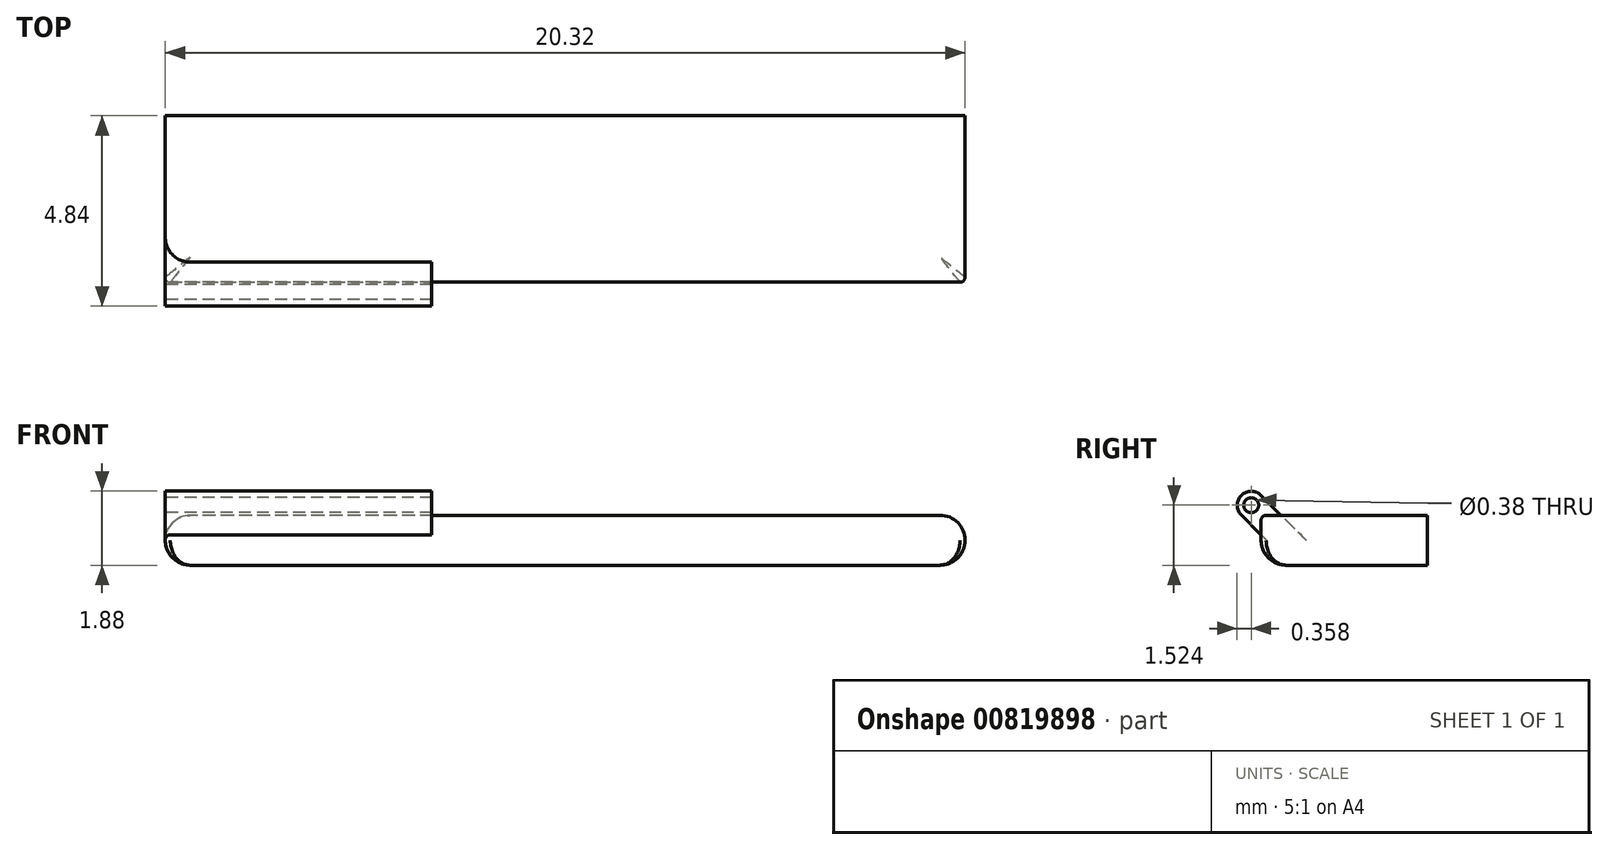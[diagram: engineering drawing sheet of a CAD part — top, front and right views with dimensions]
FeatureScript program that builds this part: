
annotation { "Feature Type Name" : "Feature", "Feature Type Description" : "" }
export const myFeature = defineFeature(function(context is Context, id is Id, definition is map)
    precondition{}
    {
        {
            var Q0;
            Q0=qCreatedBy(makeId("Top.planeOp"),FACE);
            var sketch = newSketch(context, id + "F0", { "sketchPlane" : qUnion([Q0])});
            skLineSegment(sketch, "E0.bottom", {"start": v(0, 0) * mm, "end": v(20.32, 0) * mm});
            skLineSegment(sketch, "E0.top", {"start": v(0, 8.46) * mm, "end": v(20.32, 8.46) * mm});
            skLineSegment(sketch, "E0.left", {"start": v(0, 0) * mm, "end": v(0, 8.46) * mm});
            skLineSegment(sketch, "E0.right", {"start": v(20.32, 0) * mm, "end": v(20.32, 8.46) * mm});
            skSolve(sketch);
        }
        {
            var Q0;
            Q0=qSketchRegion(id+"F0",true);
            extrude(context, id + "F1", {"entities" : qUnion([Q0]), "depth" : 1.27 * mm, "offsetDistance" : 25.4 * mm});
        }
        {
            var Q0;
            Q0=qCreatedBy(makeId("Right.planeOp"),FACE);
            var sketch = newSketch(context, id + "F2", { "sketchPlane" : qUnion([Q0])});
            skLineSegment(sketch, "E1", {"start": v(0, 1.27) * mm, "end": v(-0.25, 1.52) * mm});
            skCircle(sketch, "E2", {"center": v(-0.25, 1.52) * mm, "radius": 0.36 * mm});
            skLineSegment(sketch, "E3.0", {"start": v(0, 1.27) * mm, "end": v(8.46, 1.27) * mm});
            skLineSegment(sketch, "E4.0", {"start": v(0, 1.27) * mm, "end": v(0, 0) * mm});
            skLineSegment(sketch, "E5", {"start": v(-0.25, 1.52) * mm, "end": v(-0.5, 1.27) * mm});
            skLineSegment(sketch, "E6", {"start": v(-0.25, 1.52) * mm, "end": v(0, 1.78) * mm});
            skLineSegment(sketch, "E7", {"start": v(0, 1.78) * mm, "end": v(0.5, 1.27) * mm});
            skLineSegment(sketch, "E8", {"start": v(-0.5, 1.27) * mm, "end": v(0, 0.77) * mm});
            skSolve(sketch);
        }
        {
            var Q0;
            Q0=qSketchRegion(id+"F2",true);
            extrude(context, id + "F3", {"entities" : qUnion([Q0]), "operationType" : NewBodyOperationType.ADD, "depth" : 6.77 * mm, "offsetDistance" : 25.4 * mm});
        }
        {
            var Q0;
            Q0=makeQuery(id+"F3.boolean.opBoolean","MERGE",FACE,{"derivedFrom":[makeQuery(id+"F1.opExtrude","SWEPT_FACE",FACE,{"disambiguationData":[OSD([sQuery(id+"F0.wireOp",EDGE,"E0.left")])]}),makeQuery(id+"F3.opExtrude","CAP_FACE",FACE,{"disambiguationData":[OSD([sQuery(id+"F2.wireOp",EDGE,"E2"),sQuery(id+"F2.wireOp",EDGE,"E3.0"),sQuery(id+"F2.wireOp",EDGE,"E4.0"),sQuery(id+"F2.wireOp",EDGE,"E7"),sQuery(id+"F2.wireOp",EDGE,"E8")])],"isStart":true})]});
            cPlane(context, id + "F4", {"entities" : qUnion([Q0]), "cplaneType" : CPlaneType.OFFSET, "offset" : 10.16 * mm, "oppositeDirection" : true, "width" : 152.4 * mm, "height" : 152.4 * mm});
        }
        {
            var Q0;
            Q0=qCreatedBy(id+"F4.planeOp",FACE);
            var sketch = newSketch(context, id + "F5", { "sketchPlane" : qUnion([Q0])});
            skLineSegment(sketch, "E9.0", {"start": v(-0.5, 1.27) * mm, "end": v(-8.46, 1.27) * mm});
            skLineSegment(sketch, "E10.0", {"start": v(-8.46, 1.27) * mm, "end": v(-8.46, 0) * mm});
            skLineSegment(sketch, "E11", {"start": v(-8.46, 1.27) * mm, "end": v(-8.7, 1.52) * mm});
            skCircle(sketch, "E12", {"center": v(-8.7, 1.52) * mm, "radius": 0.36 * mm});
            skLineSegment(sketch, "E13", {"start": v(-8.7, 1.52) * mm, "end": v(-8.46, 1.77) * mm});
            skLineSegment(sketch, "E14", {"start": v(-8.46, 1.77) * mm, "end": v(-7.96, 1.27) * mm});
            skLineSegment(sketch, "E15", {"start": v(-8.7, 1.52) * mm, "end": v(-8.96, 1.27) * mm});
            skLineSegment(sketch, "E16", {"start": v(-8.96, 1.27) * mm, "end": v(-8.46, 0.77) * mm});
            skSolve(sketch);
        }
        {
            var Q0;
            Q0=qSketchRegion(id+"F5",true);
            extrude(context, id + "F6", {"entities" : qUnion([Q0]), "operationType" : NewBodyOperationType.ADD, "depth" : 3.4 * mm, "offsetDistance" : 25.4 * mm, "hasSecondDirection" : true, "secondDirectionOppositeDirection" : true, "secondDirectionDepth" : 3.4 * mm});
        }
        {
            var Q0;
            Q0=makeQuery(id+"F6.opExtrude","CAP_FACE",FACE,{"disambiguationData":[OSD([sQuery(id+"F5.wireOp",EDGE,"E9.0"),sQuery(id+"F5.wireOp",EDGE,"E10.0"),sQuery(id+"F5.wireOp",EDGE,"E12"),sQuery(id+"F5.wireOp",EDGE,"E14"),sQuery(id+"F5.wireOp",EDGE,"E16")])],"isStart":false});
            var sketch = newSketch(context, id + "F7", { "sketchPlane" : qUnion([Q0])});
            skCircle(sketch, "E17", {"center": v(-8.7, 1.52) * mm, "radius": 0.2 * mm});
            skArc(sketch, "E18.0", {"start": v(0, 1.78) * mm, "mid": v(0.5, 1.78) * mm, "end": v(0.5, 1.27) * mm});
            skCircle(sketch, "E19", {"center": v(0.25, 1.52) * mm, "radius": 0.2 * mm});
            skSolve(sketch);
        }
        {
            var Q0;
            Q0=qSketchRegion(id+"F7",true);
            extrude(context, id + "F8", {"entities" : qUnion([Q0]), "operationType" : NewBodyOperationType.REMOVE, "oppositeDirection" : true, "depth" : 25.4 * mm, "offsetDistance" : 25.4 * mm, "hasSecondDirection" : true, "secondDirectionOppositeDirection" : false, "secondDirectionDepth" : 25.4 * mm});
        }
        {
            var Q0;
            Q0=makeQuery(id+"F1.opExtrude","CAP_EDGE",EDGE,{"disambiguationData":[OSD([sQuery(id+"F0.wireOp",EDGE,"E0.bottom")])],"isStart":true});
            var Q1;
            Q1=makeQuery(id+"F1.opExtrude","CAP_EDGE",EDGE,{"disambiguationData":[OSD([sQuery(id+"F0.wireOp",EDGE,"E0.top")])],"isStart":true});
            var Q2;
            {var subQ0=sQuery(id+"F0.wireOp",EDGE,"E0.left");var subQ1=sQuery(id+"F0.wireOp",EDGE,"E0.top");Q2=makeQuery(id+"F6.boolean.opBoolean","SPLIT",EDGE,{"disambiguationData":[TD([makeQuery(id+"F1.opExtrude","SWEPT_FACE",FACE,{"disambiguationData":[OSD([subQ0])]})])],"derivedFrom":makeQuery(id+"F1.opExtrude","CAP_EDGE",EDGE,{"disambiguationData":[OSD([subQ1])],"isStart":false})});}
            var Q3;
            Q3=makeQuery(id+"F1.opExtrude","CAP_EDGE",EDGE,{"disambiguationData":[OSD([sQuery(id+"F0.wireOp",EDGE,"E0.left")])],"isStart":false});
            var Q4;
            Q4=makeQuery(id+"F1.opExtrude","CAP_EDGE",EDGE,{"disambiguationData":[OSD([sQuery(id+"F0.wireOp",EDGE,"E0.left")])],"isStart":true});
            var Q5;
            Q5=makeQuery(id+"F1.opExtrude","CAP_EDGE",EDGE,{"disambiguationData":[OSD([sQuery(id+"F0.wireOp",EDGE,"E0.right")])],"isStart":false});
            var Q6;
            Q6=makeQuery(id+"F1.opExtrude","CAP_EDGE",EDGE,{"disambiguationData":[OSD([sQuery(id+"F0.wireOp",EDGE,"E0.right")])],"isStart":true});
            fillet(context, id + "F9", {"entities" : qUnion([Q0, Q1, Q2, Q3, Q4, Q5, Q6]), "radius" : 0.64 * mm, "tangentPropagation" : true, "allowEdgeOverflow" : false});
        }
        {
            var Q0;
            Q0=makeQuery(id+"F9.opFillet","BLEND_EDGE",EDGE,{"blendedFrom":[makeQuery(id+"F1.opExtrude","CAP_EDGE",EDGE,{"disambiguationData":[OSD([sQuery(id+"F0.wireOp",EDGE,"E0.bottom")])],"isStart":true}),makeQuery(id+"F1.opExtrude","CAP_EDGE",EDGE,{"disambiguationData":[OSD([sQuery(id+"F0.wireOp",EDGE,"E0.left")])],"isStart":true})],"blendedInto":[]});
            var Q1;
            Q1=makeQuery(id+"F9.opFillet","BLEND_EDGE",EDGE,{"blendedFrom":[makeQuery(id+"F1.opExtrude","CAP_EDGE",EDGE,{"disambiguationData":[OSD([sQuery(id+"F0.wireOp",EDGE,"E0.bottom")])],"isStart":true}),makeQuery(id+"F1.opExtrude","CAP_EDGE",EDGE,{"disambiguationData":[OSD([sQuery(id+"F0.wireOp",EDGE,"E0.right")])],"isStart":true})],"blendedInto":[]});
            var Q2;
            Q2=makeQuery(id+"F9.opFillet","BLEND_EDGE",EDGE,{"blendedFrom":[makeQuery(id+"F1.opExtrude","CAP_EDGE",EDGE,{"disambiguationData":[OSD([sQuery(id+"F0.wireOp",EDGE,"E0.top")])],"isStart":true}),makeQuery(id+"F1.opExtrude","CAP_EDGE",EDGE,{"disambiguationData":[OSD([sQuery(id+"F0.wireOp",EDGE,"E0.right")])],"isStart":true})],"blendedInto":[]});
            var Q3;
            Q3=makeQuery(id+"F9.opFillet","BLEND_EDGE",EDGE,{"blendedFrom":[makeQuery(id+"F1.opExtrude","CAP_EDGE",EDGE,{"disambiguationData":[OSD([sQuery(id+"F0.wireOp",EDGE,"E0.top")])],"isStart":true}),makeQuery(id+"F1.opExtrude","CAP_EDGE",EDGE,{"disambiguationData":[OSD([sQuery(id+"F0.wireOp",EDGE,"E0.left")])],"isStart":true})],"blendedInto":[]});
            fillet(context, id + "F10", {"entities" : qUnion([Q0, Q1, Q2, Q3]), "radius" : 0.13 * mm, "tangentPropagation" : true, "allowEdgeOverflow" : false});
        }
        {
            var Q0;
            Q0=qCreatedBy(id+"F4.planeOp",FACE);
            var sketch = newSketch(context, id + "F11", { "sketchPlane" : qUnion([Q0])});
            skLineSegment(sketch, "E20.bottom", {"start": v(-4.23, 0) * mm, "end": v(-9.2, 0) * mm});
            skLineSegment(sketch, "E20.top", {"start": v(-4.23, 2.63) * mm, "end": v(-9.2, 2.63) * mm});
            skLineSegment(sketch, "E20.left", {"start": v(-4.23, 0) * mm, "end": v(-4.23, 2.63) * mm});
            skLineSegment(sketch, "E20.right", {"start": v(-9.2, 0) * mm, "end": v(-9.2, 2.63) * mm});
            skSolve(sketch);
        }
        {
            var Q0;
            Q0 = qSketchRegion(id + "F11", true);
            extrude(context, id + "F12", {"entities" : qUnion([Q0]), "operationType" : NewBodyOperationType.REMOVE, "depth" : 25.4 * mm, "offsetDistance" : 25.4 * mm, "hasSecondDirection" : true, "secondDirectionOppositeDirection" : true, "secondDirectionDepth" : 25.4 * mm});
        }
    });
